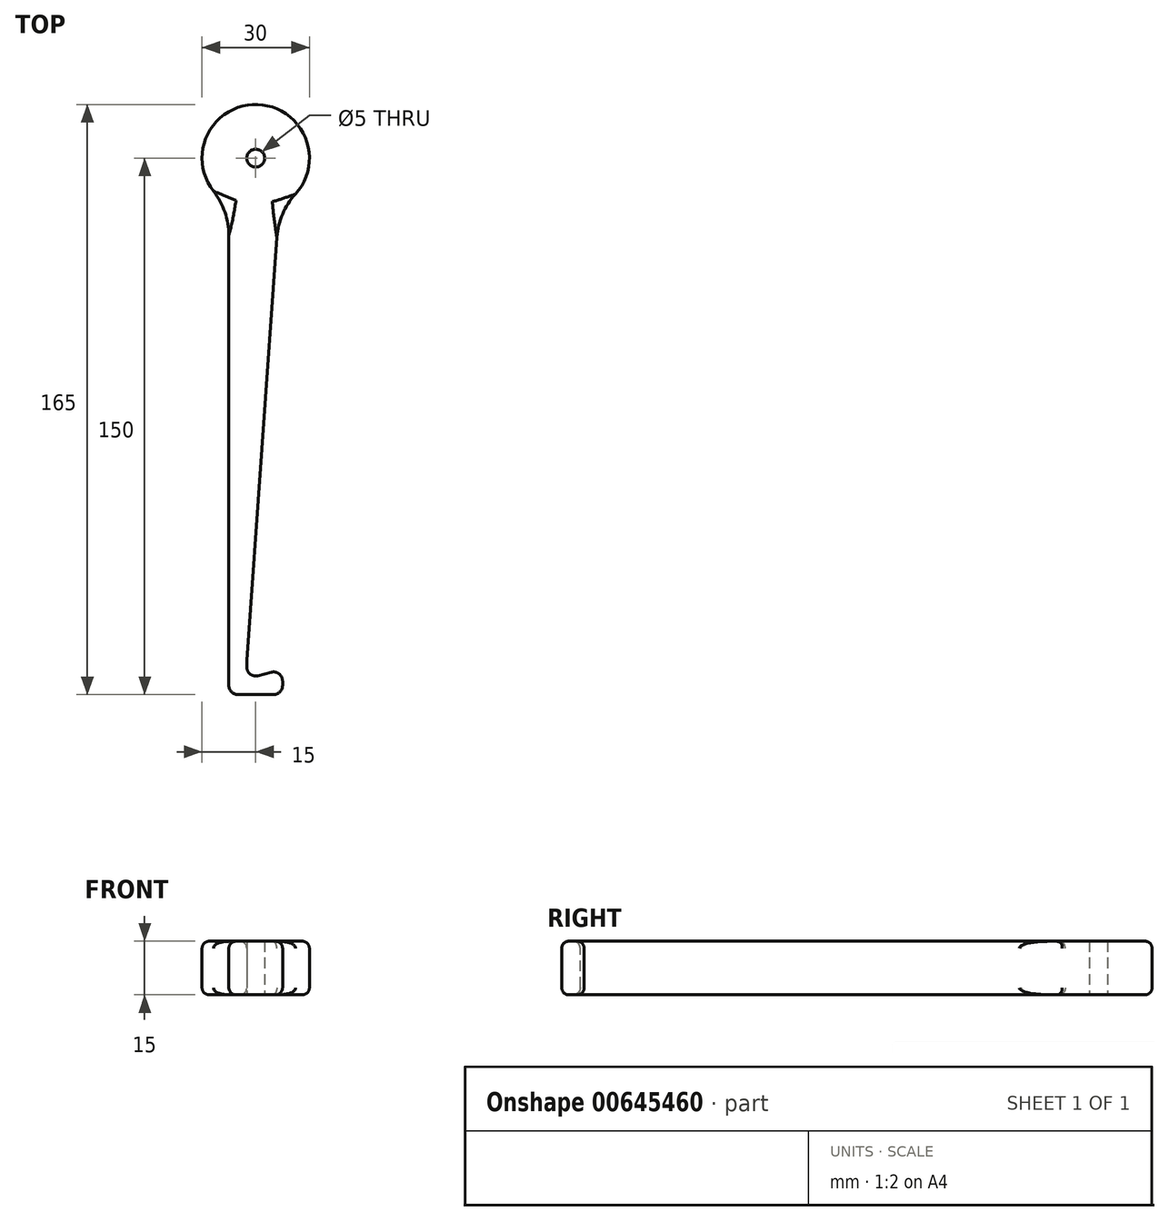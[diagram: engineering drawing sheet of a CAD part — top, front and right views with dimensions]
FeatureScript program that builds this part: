
annotation { "Feature Type Name" : "Feature", "Feature Type Description" : "" }
export const myFeature = defineFeature(function(context is Context, id is Id, definition is map)
    precondition{}
    {
        {
            var Q0;
            Q0=qCreatedBy(makeId("Top.planeOp"),FACE);
            var sketch = newSketch(context, id + "F0", { "sketchPlane" : qUnion([Q0])});
            skCircle(sketch, "E0", {"center": v(0, 0) * mm, "radius": 2.5 * mm});
            skCircle(sketch, "E1", {"center": v(0, 0) * mm, "radius": 7.5 * mm});
            skLineSegment(sketch, "E2", {"start": v(-7.5, 0) * mm, "end": v(-7.5, -150) * mm});
            skLineSegment(sketch, "E3", {"start": v(-7.5, -150) * mm, "end": v(7.5, -150) * mm});
            skLineSegment(sketch, "E4", {"start": v(-2.5, -145.53) * mm, "end": v(-2.5, -140.53) * mm});
            skLineSegment(sketch, "E5", {"start": v(-2.5, -140.53) * mm, "end": v(7.48, -0.53) * mm});
            skLineSegment(sketch, "E6", {"start": v(7.5, -150) * mm, "end": v(7.5, -143) * mm});
            skLineSegment(sketch, "E7", {"start": v(7.5, -143) * mm, "end": v(-2.5, -145.53) * mm});
            skCircle(sketch, "E8", {"center": v(0, 0) * mm, "radius": 15 * mm});
            skSolve(sketch);
        }
        {
            var Q0;
            Q0 = qSketchRegion(id + "F0", true);
            var Q1;
            Q1=makeQuery(id+"F0.imprint","IMPRINT",FACE,{"disambiguationData":[TD([[makeQuery(id+"F0.imprint","IMPRINT",EDGE,{"derivedFrom":sQuery(id+"F0.wireOp",EDGE,"E0")}),-1.0]])]});
            extrude(context, id + "F1", {"entities" : qUnion([Q0, Q1]), "depth" : 15 * mm, "offsetDistance" : 25 * mm});
        }
        {
            var Q0;
            {var subQ0=sQuery(id+"F0.wireOp",EDGE,"E2");var subQ1=sQuery(id+"F0.wireOp",EDGE,"E1");var subQ2=makeQuery(id+"F0.imprint","INTERSECT",VERTEX,{"derivedFrom":[subQ1,subQ0]});Q0=makeQuery(id+"F0.imprint","IMPRINT",FACE,{"disambiguationData":[TD([[makeQuery(id+"F0.imprint","IMPRINT",EDGE,{"disambiguationData":[TD([[subQ2,1.0]])],"derivedFrom":subQ1}),-1.0]])]});}
            extrude(context, id + "F2", {"entities" : qUnion([Q0]), "operationType" : NewBodyOperationType.ADD, "depth" : 15 * mm, "offsetDistance" : 25 * mm});
        }
        {
            var Q0;
            Q0=makeQuery(id+"F1.opExtrude","SWEPT_EDGE",EDGE,{"disambiguationData":[OSD([sQuery(id+"F0.wireOp",EDGE,"E6"),sQuery(id+"F0.wireOp",EDGE,"E7")])]});
            var Q1;
            Q1=makeQuery(id+"F1.opExtrude","SWEPT_EDGE",EDGE,{"disambiguationData":[OSD([sQuery(id+"F0.wireOp",EDGE,"E3"),sQuery(id+"F0.wireOp",EDGE,"E6")])]});
            var Q2;
            Q2=makeQuery(id+"F1.opExtrude","SWEPT_EDGE",EDGE,{"disambiguationData":[OSD([sQuery(id+"F0.wireOp",EDGE,"E4"),sQuery(id+"F0.wireOp",EDGE,"E7")])]});
            var Q3;
            Q3=makeQuery(id+"F1.opExtrude","SWEPT_EDGE",EDGE,{"disambiguationData":[OSD([sQuery(id+"F0.wireOp",EDGE,"E4"),sQuery(id+"F0.wireOp",EDGE,"E5")])]});
            var Q4;
            Q4=makeQuery(id+"F1.opExtrude","SWEPT_EDGE",EDGE,{"disambiguationData":[OSD([sQuery(id+"F0.wireOp",EDGE,"E2"),sQuery(id+"F0.wireOp",EDGE,"E3")])]});
            fillet(context, id + "F3", {"entities" : qUnion([Q0, Q1, Q2, Q3, Q4]), "radius" : 2.5 * mm, "tangentPropagation" : true, "allowEdgeOverflow" : false});
        }
        {
            var Q0;
            Q0=makeQuery(id+"F1.opExtrude","CAP_EDGE",EDGE,{"disambiguationData":[OSD([sQuery(id+"F0.wireOp",EDGE,"E5")])],"isStart":false});
            var Q1;
            {var subQ0=sQuery(id+"F0.wireOp",EDGE,"E7");var subQ1=sQuery(id+"F0.wireOp",EDGE,"E4");Q1=makeQuery(id+"F3.opFillet","BLEND_EDGE",EDGE,{"blendedFrom":[makeQuery(id+"F1.opExtrude","SWEPT_EDGE",EDGE,{"disambiguationData":[OSD([subQ1,subQ0])]}),makeQuery(id+"F1.opExtrude","CAP_FACE",FACE,{"disambiguationData":[OSD([sQuery(id+"F0.wireOp",EDGE,"E0"),sQuery(id+"F0.wireOp",EDGE,"E1"),sQuery(id+"F0.wireOp",EDGE,"E2"),sQuery(id+"F0.wireOp",EDGE,"E3"),subQ1,sQuery(id+"F0.wireOp",EDGE,"E5"),sQuery(id+"F0.wireOp",EDGE,"E6"),subQ0])],"isStart":false})],"blendedInto":[makeQuery(id+"F1.opExtrude","CAP_FACE",FACE,{"disambiguationData":[OSD([sQuery(id+"F0.wireOp",EDGE,"E0"),sQuery(id+"F0.wireOp",EDGE,"E1"),sQuery(id+"F0.wireOp",EDGE,"E2"),sQuery(id+"F0.wireOp",EDGE,"E3"),subQ1,sQuery(id+"F0.wireOp",EDGE,"E5"),sQuery(id+"F0.wireOp",EDGE,"E6"),subQ0])],"isStart":false})]});}
            var Q2;
            Q2=makeQuery(id+"F1.opExtrude","CAP_EDGE",EDGE,{"disambiguationData":[OSD([sQuery(id+"F0.wireOp",EDGE,"E7")])],"isStart":false});
            var Q3;
            {var subQ0=sQuery(id+"F0.wireOp",EDGE,"E7");var subQ1=sQuery(id+"F0.wireOp",EDGE,"E6");Q3=makeQuery(id+"F3.opFillet","BLEND_EDGE",EDGE,{"blendedFrom":[makeQuery(id+"F1.opExtrude","SWEPT_EDGE",EDGE,{"disambiguationData":[OSD([subQ1,subQ0])]}),makeQuery(id+"F1.opExtrude","CAP_FACE",FACE,{"disambiguationData":[OSD([sQuery(id+"F0.wireOp",EDGE,"E0"),sQuery(id+"F0.wireOp",EDGE,"E1"),sQuery(id+"F0.wireOp",EDGE,"E2"),sQuery(id+"F0.wireOp",EDGE,"E3"),sQuery(id+"F0.wireOp",EDGE,"E4"),sQuery(id+"F0.wireOp",EDGE,"E5"),subQ1,subQ0])],"isStart":false})],"blendedInto":[makeQuery(id+"F1.opExtrude","CAP_FACE",FACE,{"disambiguationData":[OSD([sQuery(id+"F0.wireOp",EDGE,"E0"),sQuery(id+"F0.wireOp",EDGE,"E1"),sQuery(id+"F0.wireOp",EDGE,"E2"),sQuery(id+"F0.wireOp",EDGE,"E3"),sQuery(id+"F0.wireOp",EDGE,"E4"),sQuery(id+"F0.wireOp",EDGE,"E5"),subQ1,subQ0])],"isStart":false})]});}
            var Q4;
            {var subQ0=sQuery(id+"F0.wireOp",EDGE,"E6");var subQ1=sQuery(id+"F0.wireOp",EDGE,"E3");Q4=makeQuery(id+"F3.opFillet","BLEND_EDGE",EDGE,{"blendedFrom":[makeQuery(id+"F1.opExtrude","SWEPT_EDGE",EDGE,{"disambiguationData":[OSD([subQ1,subQ0])]}),makeQuery(id+"F1.opExtrude","CAP_FACE",FACE,{"disambiguationData":[OSD([sQuery(id+"F0.wireOp",EDGE,"E0"),sQuery(id+"F0.wireOp",EDGE,"E1"),sQuery(id+"F0.wireOp",EDGE,"E2"),subQ1,sQuery(id+"F0.wireOp",EDGE,"E4"),sQuery(id+"F0.wireOp",EDGE,"E5"),subQ0,sQuery(id+"F0.wireOp",EDGE,"E7")])],"isStart":false})],"blendedInto":[makeQuery(id+"F1.opExtrude","CAP_FACE",FACE,{"disambiguationData":[OSD([sQuery(id+"F0.wireOp",EDGE,"E0"),sQuery(id+"F0.wireOp",EDGE,"E1"),sQuery(id+"F0.wireOp",EDGE,"E2"),subQ1,sQuery(id+"F0.wireOp",EDGE,"E4"),sQuery(id+"F0.wireOp",EDGE,"E5"),subQ0,sQuery(id+"F0.wireOp",EDGE,"E7")])],"isStart":false})]});}
            var Q5;
            Q5=makeQuery(id+"F1.opExtrude","CAP_EDGE",EDGE,{"disambiguationData":[OSD([sQuery(id+"F0.wireOp",EDGE,"E3")])],"isStart":false});
            var Q6;
            {var subQ0=sQuery(id+"F0.wireOp",EDGE,"E3");var subQ1=sQuery(id+"F0.wireOp",EDGE,"E2");Q6=makeQuery(id+"F3.opFillet","BLEND_EDGE",EDGE,{"blendedFrom":[makeQuery(id+"F1.opExtrude","SWEPT_EDGE",EDGE,{"disambiguationData":[OSD([subQ1,subQ0])]}),makeQuery(id+"F1.opExtrude","CAP_FACE",FACE,{"disambiguationData":[OSD([sQuery(id+"F0.wireOp",EDGE,"E0"),sQuery(id+"F0.wireOp",EDGE,"E1"),subQ1,subQ0,sQuery(id+"F0.wireOp",EDGE,"E4"),sQuery(id+"F0.wireOp",EDGE,"E5"),sQuery(id+"F0.wireOp",EDGE,"E6"),sQuery(id+"F0.wireOp",EDGE,"E7")])],"isStart":false})],"blendedInto":[makeQuery(id+"F1.opExtrude","CAP_FACE",FACE,{"disambiguationData":[OSD([sQuery(id+"F0.wireOp",EDGE,"E0"),sQuery(id+"F0.wireOp",EDGE,"E1"),subQ1,subQ0,sQuery(id+"F0.wireOp",EDGE,"E4"),sQuery(id+"F0.wireOp",EDGE,"E5"),sQuery(id+"F0.wireOp",EDGE,"E6"),sQuery(id+"F0.wireOp",EDGE,"E7")])],"isStart":false})]});}
            var Q7;
            Q7=makeQuery(id+"F1.opExtrude","CAP_EDGE",EDGE,{"disambiguationData":[OSD([sQuery(id+"F0.wireOp",EDGE,"E2")])],"isStart":false});
            var Q8;
            Q8=makeQuery(id+"F1.opExtrude","CAP_EDGE",EDGE,{"disambiguationData":[OSD([sQuery(id+"F0.wireOp",EDGE,"E4")])],"isStart":false});
            var Q9;
            Q9=makeQuery(id+"F1.opExtrude","CAP_EDGE",EDGE,{"disambiguationData":[OSD([sQuery(id+"F0.wireOp",EDGE,"E6")])],"isStart":false});
            var Q10;
            Q10=makeQuery(id+"F1.opExtrude","CAP_EDGE",EDGE,{"disambiguationData":[OSD([sQuery(id+"F0.wireOp",EDGE,"E5")])],"isStart":true});
            var Q11;
            Q11=makeQuery(id+"F1.opExtrude","CAP_EDGE",EDGE,{"disambiguationData":[OSD([sQuery(id+"F0.wireOp",EDGE,"E8")])],"isStart":false});
            var Q12;
            Q12=makeQuery(id+"F1.opExtrude","CAP_EDGE",EDGE,{"disambiguationData":[OSD([sQuery(id+"F0.wireOp",EDGE,"E8")])],"isStart":true});
            fillet(context, id + "F4", {"entities" : qUnion([Q0, Q1, Q2, Q3, Q4, Q5, Q6, Q7, Q8, Q9, Q10, Q11, Q12]), "radius" : 2 * mm, "tangentPropagation" : true, "allowEdgeOverflow" : false});
        }
        {
            var Q0;
            Q0=makeQuery(id+"F1.opExtrude","SWEPT_EDGE",EDGE,{"disambiguationData":[OSD([sQuery(id+"F0.wireOp",EDGE,"E5"),sQuery(id+"F0.wireOp",EDGE,"E8")])]});
            var Q1;
            Q1=makeQuery(id+"F1.opExtrude","SWEPT_EDGE",EDGE,{"disambiguationData":[OSD([sQuery(id+"F0.wireOp",EDGE,"E2"),sQuery(id+"F0.wireOp",EDGE,"E8")])]});
            fillet(context, id + "F5", {"entities" : qUnion([Q0, Q1]), "radius" : 20 * mm, "tangentPropagation" : true, "allowEdgeOverflow" : false});
        }
    });
